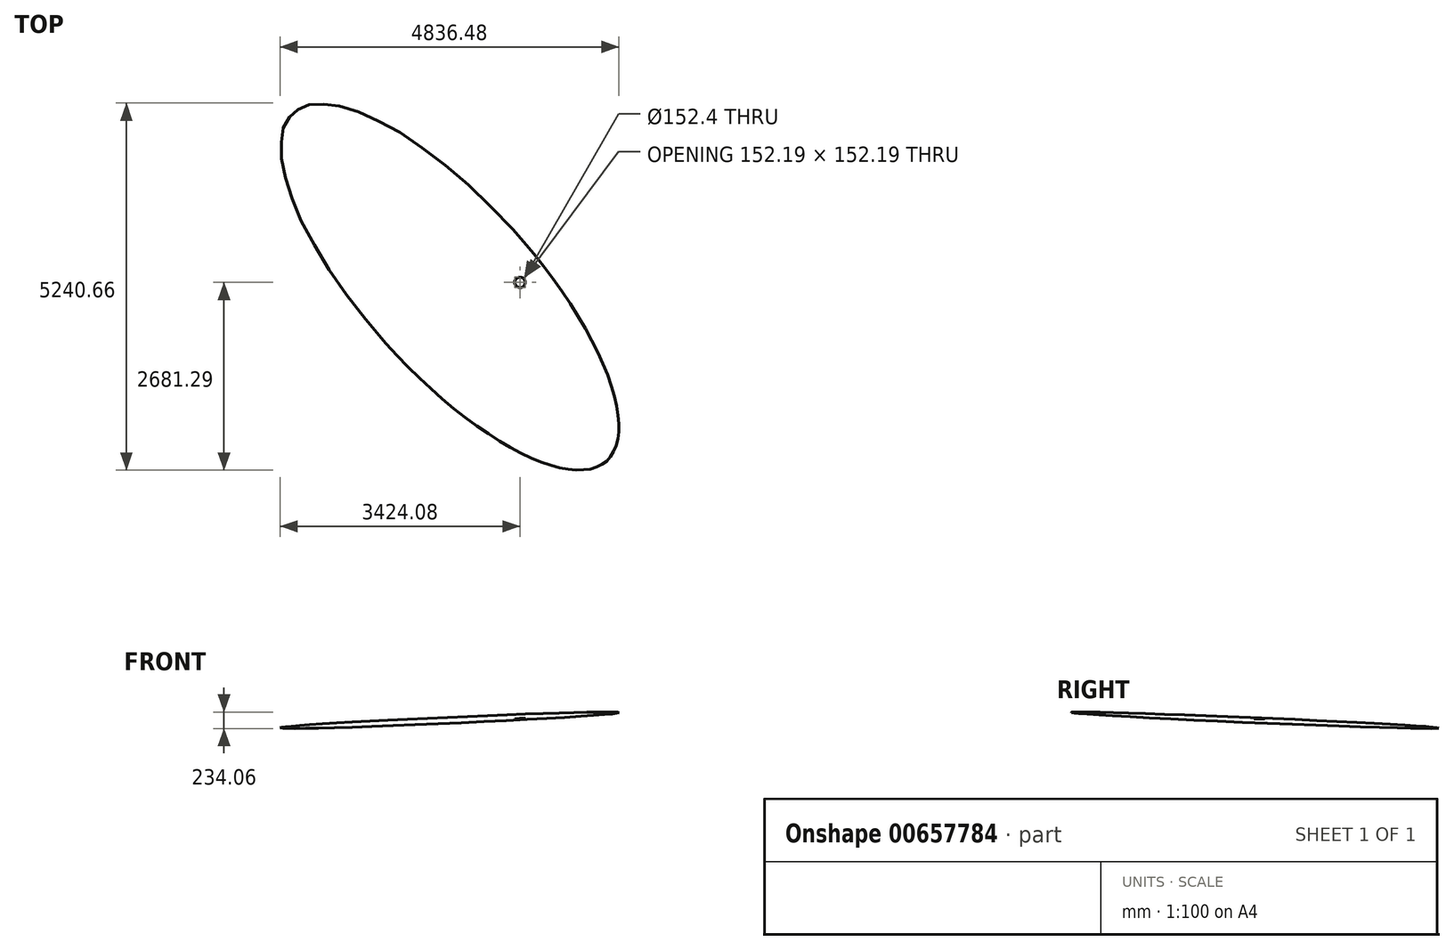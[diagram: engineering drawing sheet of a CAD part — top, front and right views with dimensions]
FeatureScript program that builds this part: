
annotation { "Feature Type Name" : "Feature", "Feature Type Description" : "" }
export const myFeature = defineFeature(function(context is Context, id is Id, definition is map)
    precondition{}
    {
        {
            assignVariable(context, id + "F0", {"name" : "Azimuth", "anyValue" : 228});
        }
        {
            assignVariable(context, id + "F1", {"name" : "Dip", "anyValue" : 2});
        }
        {
            assignVariable(context, id + "F2", {"name" : "Width", "anyValue" : 0.04});
        }
        {
            var Q0;
            Q0=qCreatedBy(makeId("Top.planeOp"),FACE);
            var sketch = newSketch(context, id + "F3", { "sketchPlane" : qUnion([Q0])});
            skEllipse(sketch, "E0", {"center": v(0, 0) * mm, "majorRadius": 1219.2 * mm, "minorRadius": 3352.8 * mm, "majorAxis": v(0, 1)});
            skLineSegment(sketch, "E1", {"start": v(0, 1874.52) * mm, "end": v(0, -1874.52) * mm, "construction": true});
            skLineSegment(sketch, "E2", {"start": v(-1173.48, 0) * mm, "end": v(1173.48, 0) * mm, "construction": true});
            skLineSegment(sketch, "E3.0", {"start": v(-1005.84, 1219.2) * mm, "end": v(-1005.84, -1219.2) * mm, "construction": true});
            skLineSegment(sketch, "E4.0", {"start": v(-3352.8, 60.96) * mm, "end": v(3352.8, 60.96) * mm, "construction": true});
            skSolve(sketch);
        }
        {
            var Q0;
            Q0=qCreatedBy(makeId("Top.planeOp"),FACE);
            var sketch = newSketch(context, id + "F4", { "sketchPlane" : qUnion([Q0])});
            skLineSegment(sketch, "E5", {"start": v(-1005.84, 0) * mm, "end": v(0, 0) * mm});
            skLineSegment(sketch, "E6", {"start": v(-1005.84, 60.96) * mm, "end": v(-1005.84, 0) * mm});
            skSolve(sketch);
        }
        {
            var Q0;
            Q0=qSketchRegion(id+"F3",true);
            extrude(context, id + "F5", {"entities" : qUnion([Q0]), "depth" : (getVariable(context, 'Width')) * mm});
        }
        {
            var Q0;
            Q0=qCreatedBy(makeId("Front.planeOp"),FACE);
            var sketch = newSketch(context, id + "F6", { "sketchPlane" : qUnion([Q0])});
            skLineSegment(sketch, "E7", {"start": v(0, 0) * mm, "end": v(0, -5486.4) * mm, "construction": true});
            skSolve(sketch);
        }
        {
            var Q0;
            Q0=makeQuery(id+"F5.opExtrude","SWEPT_BODY",BODY,{"disambiguationData":[OSD([sQuery(id+"F3.wireOp",EDGE,"E0"),sQuery(id+"F3.wireOp",EDGE,"TMMzbr5i-4nV4-ZnMr-aG6B-IGJ66UyS6uPJ")])]});
            var Q1;
            Q1=sQuery(id+"F3.wireOp",EDGE,"E1");
            transform(context, id + "F7", {"entities" : qUnion([Q0]), "transformType" : TransformType.ROTATION, "transformAxis" : qUnion([Q1]), "angle" : (getVariable(context, 'Dip')) * degree, "oppositeDirection" : true, "makeCopy" : false});
        }
        {
            var Q0;
            Q0=makeQuery(id+"F5.opExtrude","SWEPT_BODY",BODY,{"disambiguationData":[OSD([sQuery(id+"F3.wireOp",EDGE,"E0")])]});
            var Q1;
            Q1=sQuery(id+"F6.wireOp",EDGE,"E7");
            transform(context, id + "F8", {"entities" : qUnion([Q0]), "transformType" : TransformType.ROTATION, "transformAxis" : qUnion([Q1]), "angle" : (getVariable(context, 'Azimuth')) * degree, "makeCopy" : false});
        }
        {
            var Q0;
            Q0=makeQuery(id+"F5.opExtrude","SWEPT_BODY",BODY,{"disambiguationData":[OSD([sQuery(id+"F3.wireOp",EDGE,"E0"),sQuery(id+"F3.wireOp",EDGE,"TMMzbr5i-4nV4-ZnMr-aG6B-IGJ66UyS6uPJ")])]});
            var Q1;
            Q1=sQuery(id+"F4.wireOp",EDGE,"E5");
            transform(context, id + "F9", {"entities" : qUnion([Q0]), "transformType" : TransformType.TRANSLATION_ENTITY, "oppositeDirectionEntity" : true, "transformLine" : qUnion([Q1]), "makeCopy" : false});
        }
        {
            var Q0;
            Q0=makeQuery(id+"F5.opExtrude","SWEPT_BODY",BODY,{"disambiguationData":[OSD([sQuery(id+"F3.wireOp",EDGE,"E0"),sQuery(id+"F3.wireOp",EDGE,"TMMzbr5i-4nV4-ZnMr-aG6B-IGJ66UyS6uPJ")])]});
            var Q1;
            Q1=sQuery(id+"F4.wireOp",EDGE,"E6");
            transform(context, id + "F10", {"entities" : qUnion([Q0]), "transformType" : TransformType.TRANSLATION_ENTITY, "oppositeDirectionEntity" : false, "transformLine" : qUnion([Q1]), "makeCopy" : false});
        }
        {
            var Q0;
            Q0=qCreatedBy(makeId("Top.planeOp"),FACE);
            var sketch = newSketch(context, id + "F11", { "sketchPlane" : qUnion([Q0])});
            skCircle(sketch, "E8", {"center": v(0, 0) * mm, "radius": 76.2 * mm});
            skSolve(sketch);
        }
        {
            var Q0;
            Q0=qSketchRegion(id+"F11",true);
            extrude(context, id + "F12", {"entities" : qUnion([Q0]), "operationType" : NewBodyOperationType.REMOVE, "endBound" : BoundingType.THROUGH_ALL, "oppositeDirection" : true, "depth" : 30.48 * mm, "hasSecondDirection" : true, "secondDirectionBound" : SecondDirectionBoundingType.THROUGH_ALL, "secondDirectionOppositeDirection" : false, "secondDirectionDepth" : 30.48 * mm});
        }
        {
            var Q0;
            Q0=qCreatedBy(makeId("Front.planeOp"),FACE);
            var sketch = newSketch(context, id + "F13", { "sketchPlane" : qUnion([Q0])});
            skLineSegment(sketch, "E9", {"start": v(0, 21.92) * mm, "end": v(0, -5486.4) * mm});
            skSolve(sketch);
        }
        {
            var Q0;
            Q0=makeQuery(id+"F5.opExtrude","SWEPT_BODY",BODY,{"disambiguationData":[OSD([sQuery(id+"F3.wireOp",EDGE,"E0")])]});
            var Q1;
            Q1=sQuery(id+"F13.wireOp",EDGE,"E9");
            transform(context, id + "F14", {"entities" : qUnion([Q0]), "transformType" : TransformType.TRANSLATION_ENTITY, "oppositeDirectionEntity" : false, "transformLine" : qUnion([Q1]), "makeCopy" : false});
        }
    });
